# Revit family: BRG-GRF-CCN_BELFORT MONOMANDO ALTO PARA COCINA CROMO
name_source: partatom
category: Aparatos sanitarios
units: mm (PartAtom-declared; Revit-internal decimal feet)

## family parameters
Compartido = Sí
Corte con vacíos al cargar = No
Cota de conector redondo = Diámetro de uso
Número OmniClass = 23.45.00.00
Punto de cálculo de habitación = Sí
Se basa en plano de trabajo = No
Siempre vertical = Sí
Tipo de pieza = Normal
Título OmniClass = Sanitary, Laundry, and Cleaning Equipment

## types (1)
- BELFORT MONOMANDO ALTO PARA COCINA
    Conexión AC = Sí
    Conexión AF = Sí
    Conexión de residuos = Sí
    Conexión de ventilación = Sí
    Fabricante = BRIGGS Ecuador
    Imagen de tipo = <Ninguno>
    Modelo = BELFORT MONOMANDO ALTO PARA COCINA
    URL = https://www.briggs.com.ec
    _ALT_Meson = 0.85 m
    _ALT_Toma = 0.55 m
    _EDESA_ Alto en cm = 30.5
    _EDESA_ Ancho en cm = 22
    _EDESA_ Categoría = Productos > Grifería > Cocina
    _EDESA_ Certificación = Cumple con norma NTE - INEN 3123 basada en la norma ASME 112.18.1 - 2012. Nuestras mangueras cuentan certificación cUPC.
    _EDESA_ Color = Cromo
    _EDESA_ Conexión hidráulica = Entrada de agua: tubería ø 1/2" Salida de agua: tubería PVC 50
    _EDESA_ Consumo/capacidad de agua en L = 8.3 litros por minuto / 2.2 gpm a 60 psi
    _EDESA_ Descripción = Grifería monomando de cocina para agua fría y caliente. Instalación sobre fregadero o mesón. Incluye mangueras flexibles.
    _EDESA_ Garantía = De por vida para el cuerpo principal y acabado en cromo (306)
    _EDESA_ Manual de instalación = https://www.briggs.com.ec
    _EDESA_ Marca = BRIGGS
    _EDESA_ Materiales = Latón
    _EDESA_ Nombre = BELFORT MONOMANDO ALTO PARA COCINA
    _EDESA_ Productos incluídos = 2 Mangueras monomando 16"
    _EDESA_ Productos necesarios para instalación = Desagüe y Sifón para fregadero
    _EDESA_ Profundidad en cm = 14
    _EDESA_ Sku/código = SG0081553061CW
    _EDESA_ Tipo de instalación = Sobre fregadero o mesón
